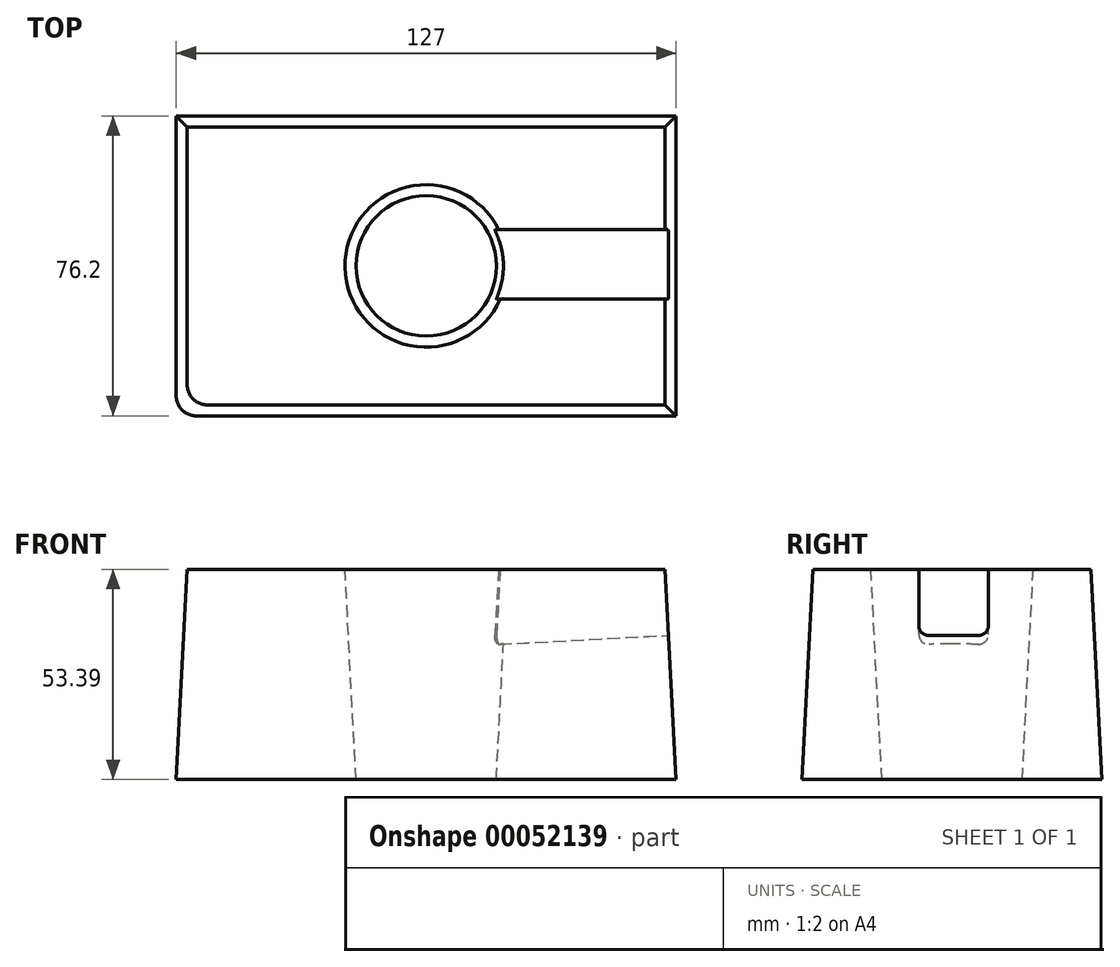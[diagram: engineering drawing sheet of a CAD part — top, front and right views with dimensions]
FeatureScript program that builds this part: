
annotation { "Feature Type Name" : "Feature", "Feature Type Description" : "" }
export const myFeature = defineFeature(function(context is Context, id is Id, definition is map)
    precondition{}
    {
        {
            var Q0;
            Q0=qCreatedBy(makeId("Top.planeOp"),FACE);
            var sketch = newSketch(context, id + "F0", { "sketchPlane" : qUnion([Q0])});
            skLineSegment(sketch, "E0.bottom", {"start": v(-129.05, 76.57) * mm, "end": v(-2.05, 76.57) * mm});
            skLineSegment(sketch, "E0.top", {"start": v(-129.05, 0.37) * mm, "end": v(-2.05, 0.37) * mm});
            skLineSegment(sketch, "E0.left", {"start": v(-129.05, 76.57) * mm, "end": v(-129.05, 0.37) * mm});
            skLineSegment(sketch, "E0.right", {"start": v(-2.05, 76.57) * mm, "end": v(-2.05, 0.37) * mm});
            skCircle(sketch, "E1", {"center": v(-65.55, 38.47) * mm, "radius": 17.83 * mm});
            skSolve(sketch);
        }
        {
            var Q0;
            Q0 = qSketchRegion(id + "F0", true);
            extrude(context, id + "F1", {"entities" : qUnion([Q0]), "depth" : 53.4 * mm, "hasDraft" : true, "draftAngle" : 3 * degree, "draftPullDirection" : true});
        }
        {
            var Q0;
            Q0=makeQuery(id+"F1.opExtrude","SWEPT_EDGE",EDGE,{"disambiguationData":[OSD([sQuery(id+"F0.wireOp",EDGE,"E0.top"),sQuery(id+"F0.wireOp",EDGE,"E0.left")])]});
            fillet(context, id + "F2", {"entities" : qUnion([Q0]), "radius" : 5.08 * mm, "tangentPropagation" : true, "allowEdgeOverflow" : false});
        }
        {
            var Q0;
            Q0=makeQuery(id+"F1.opExtrude","SWEPT_FACE",FACE,{"disambiguationData":[OSD([sQuery(id+"F0.wireOp",EDGE,"E0.right")])]});
            var sketch = newSketch(context, id + "F3", { "sketchPlane" : qUnion([Q0])});
            skLineSegment(sketch, "E2.bottom", {"start": v(30.02, 62.37) * mm, "end": v(47.72, 62.37) * mm});
            skLineSegment(sketch, "E2.top", {"start": v(30.02, 36.78) * mm, "end": v(47.72, 36.78) * mm});
            skLineSegment(sketch, "E2.left", {"start": v(30.02, 62.37) * mm, "end": v(30.02, 36.78) * mm});
            skLineSegment(sketch, "E2.right", {"start": v(47.72, 62.37) * mm, "end": v(47.72, 36.78) * mm});
            skSolve(sketch);
        }
        {
            var Q0;
            Q0 = qSketchRegion(id + "F3", true);
            var Q1;
            Q1=makeQuery(id+"F1.opExtrude","SWEPT_FACE",FACE,{"disambiguationData":[OSD([sQuery(id+"F0.wireOp",EDGE,"E1")])]});
            extrude(context, id + "F4", {"entities" : qUnion([Q0]), "operationType" : NewBodyOperationType.REMOVE, "endBound" : BoundingType.UP_TO_SURFACE, "oppositeDirection" : true, "endBoundEntityFace" : qUnion([Q1]), "depth" : 56.63 * mm});
        }
        {
            var Q0;
            Q0=makeQuery(id+"F4.boolean.opBoolean","COPY",EDGE,{"derivedFrom":makeQuery(id+"F4.opExtrude","CAP_EDGE",EDGE,{"disambiguationData":[OSD([sQuery(id+"F3.wireOp",EDGE,"E2.right")])],"isStart":false})});
            var Q1;
            Q1=makeQuery(id+"F4.boolean.opBoolean","COPY",EDGE,{"derivedFrom":makeQuery(id+"F4.opExtrude","SWEPT_EDGE",EDGE,{"disambiguationData":[OSD([sQuery(id+"F3.wireOp",EDGE,"E2.top"),sQuery(id+"F3.wireOp",EDGE,"E2.right")])]})});
            var Q2;
            Q2=makeQuery(id+"F4.boolean.opBoolean","COPY",EDGE,{"derivedFrom":makeQuery(id+"F4.opExtrude","SWEPT_EDGE",EDGE,{"disambiguationData":[OSD([sQuery(id+"F3.wireOp",EDGE,"E2.top"),sQuery(id+"F3.wireOp",EDGE,"E2.left")])]})});
            fillet(context, id + "F5", {"entities" : qUnion([Q0, Q1, Q2]), "radius" : 2.54 * mm, "tangentPropagation" : true, "allowEdgeOverflow" : false});
        }
    });
